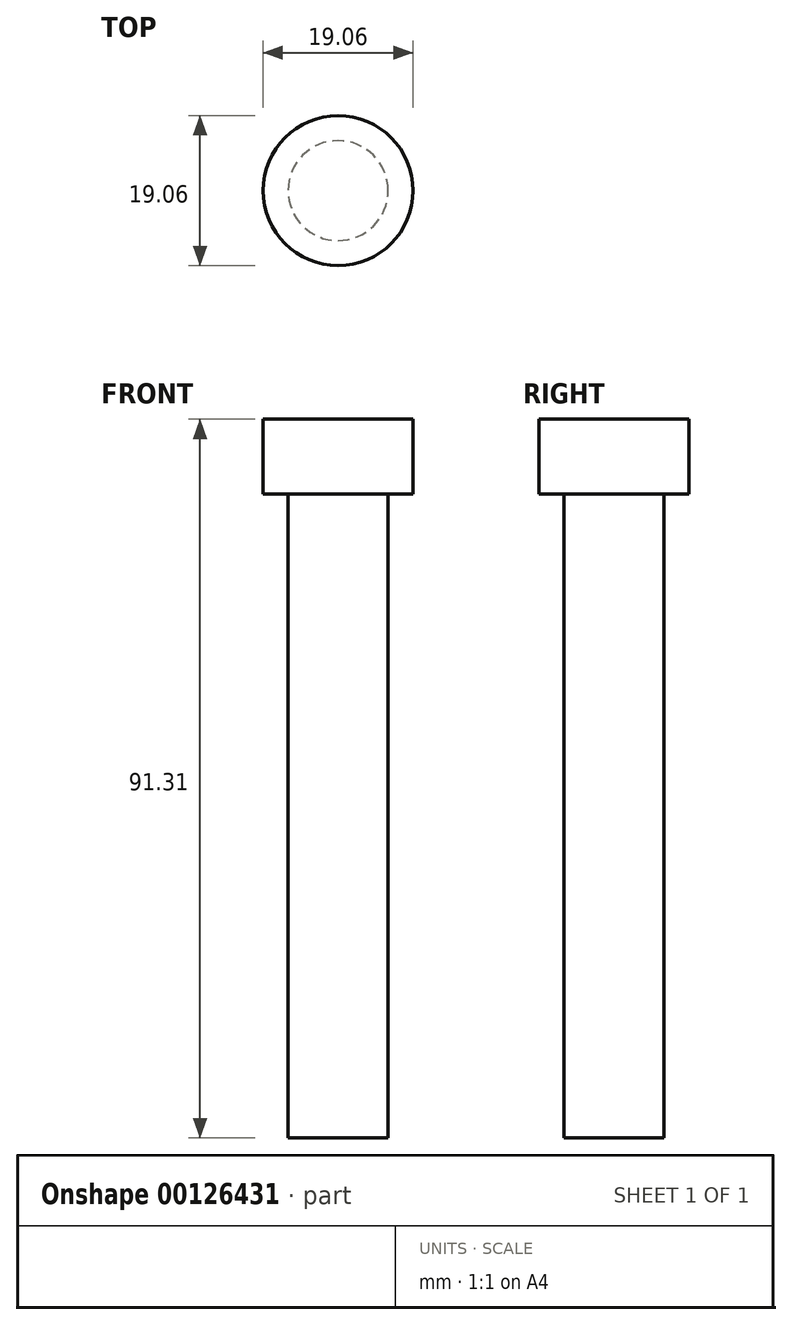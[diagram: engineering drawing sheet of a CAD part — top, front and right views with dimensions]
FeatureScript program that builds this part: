
annotation { "Feature Type Name" : "Feature", "Feature Type Description" : "" }
export const myFeature = defineFeature(function(context is Context, id is Id, definition is map)
    precondition{}
    {
        {
            var Q0;
            Q0=qCreatedBy(makeId("Right.planeOp"),FACE);
            var sketch = newSketch(context, id + "F0", { "sketchPlane" : qUnion([Q0])});
            skLineSegment(sketch, "E0", {"start": v(0, 0) * mm, "end": v(-9.53, 0) * mm});
            skLineSegment(sketch, "E1", {"start": v(-9.53, 0) * mm, "end": v(-9.53, -9.53) * mm});
            skLineSegment(sketch, "E2", {"start": v(-9.53, -9.53) * mm, "end": v(-6.35, -9.53) * mm});
            skLineSegment(sketch, "E3", {"start": v(-6.35, -9.53) * mm, "end": v(-6.35, -91.31) * mm});
            skLineSegment(sketch, "E4", {"start": v(-6.35, -91.31) * mm, "end": v(0, -91.31) * mm});
            skLineSegment(sketch, "E5", {"start": v(0, -91.31) * mm, "end": v(0, 0) * mm});
            skSolve(sketch);
        }
        {
            var Q0;
            Q0=makeQuery(id+"F0.imprint","IMPRINT",FACE,{"disambiguationData":[TD([[makeQuery(id+"F0.imprint","IMPRINT",EDGE,{"derivedFrom":sQuery(id+"F0.wireOp",EDGE,"E0")}),1.0]])]});
            var Q1;
            Q1=sQuery(id+"F0.wireOp",EDGE,"E5");
            revolve(context, id + "F1", {"entities" : qUnion([Q0]), "axis" : qUnion([Q1]), "revolveType" : RevolveType.FULL});
        }
    });
